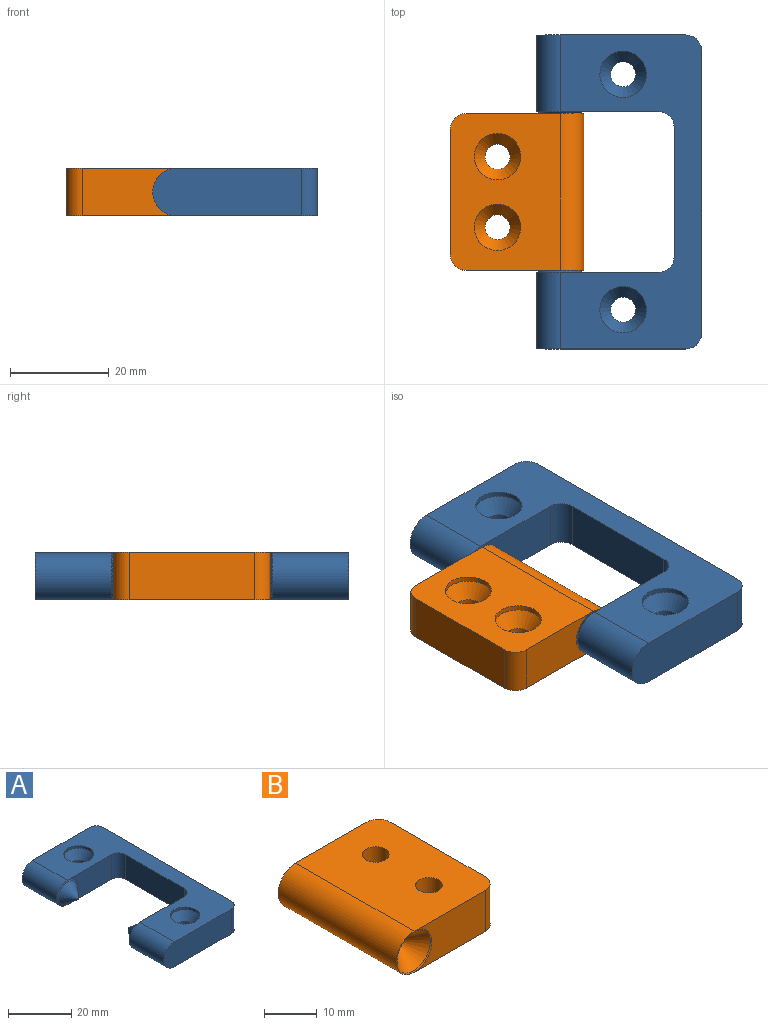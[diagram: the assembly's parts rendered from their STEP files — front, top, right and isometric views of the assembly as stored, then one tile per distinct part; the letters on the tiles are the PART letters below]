
ASSEMBLY  parts=2 mates=1
PART A: 26 faces, bbox 34.3x63.5x11.5 mm
  f0: plane 19.84x9.53mm, normal (0,-1,0), area 153.4mm2, adj f4,f6,f19,f23
  f1: plane 19.84x9.53mm, normal (0,1,0), area 153.4mm2, adj f4,f6,f18,f22
  f2: cylinder r=4.76mm len=15.48mm, axis (0,1,0), area 231.6mm2, adj f4,f6,f8,f19
  f3: cylinder r=4.76mm len=15.48mm, axis (0,1,0), area 231.6mm2, adj f4,f6,f7,f18
  f4: plane 63.5x28.58mm, normal (0,0,-1), area 1024.9mm2, adj f0,f1,f2,f3,f5,f7,f8,f9
  f5: plane 57.15x9.53mm, normal (1,0,0), area 544.4mm2, adj f4,f6,f24,f25
  f6: plane 63.5x28.58mm, normal (0,0,1), area 926.7mm2, adj f0,f1,f2,f3,f5,f7,f8,f9
  f7: plane 30.16x9.53mm, normal (0,-1,0), area 277.6mm2, adj f3,f4,f6,f25
  f8: plane 30.16x9.53mm, normal (0,1,0), area 277.6mm2, adj f2,f4,f6,f24
  f9: plane 26.19x9.53mm, normal (-1,0,0), area 249.5mm2, adj f4,f6,f22,f23
  f10: cylinder r=2.54mm len=5.43mm, axis (0,0,1), area 86.6mm2, adj f4,f11
  f11: cone r=4.7mm half-angle=35deg, axis (0,0,1), area 85.6mm2, adj f10,f12
  f12: cylinder r=4.7mm len=9.4mm, axis (0,0,1), area 30mm2, adj f6,f11
  f13: cylinder r=2.54mm len=5.43mm, axis (0,0,1), area 86.6mm2, adj f4,f14
  f14: cone r=4.7mm half-angle=35deg, axis (0,0,1), area 85.6mm2, adj f13,f15
  f15: cylinder r=4.7mm len=9.4mm, axis (0,0,1), area 30mm2, adj f6,f14
  f16: sphere r=0.4mm, area 0.4mm2, adj f17
  f17: cone r=4.15mm half-angle=40deg, axis (0,-1,0), area 83.9mm2, adj f16,f18
  f18: torus R=4.76mm, axis (0,1,0), area 19.3mm2, adj f1,f3,f17
  f19: torus R=4.76mm, axis (0,1,0), area 19.3mm2, adj f0,f2,f20
  f20: cone r=4.15mm half-angle=40deg, axis (0,1,0), area 83.9mm2, adj f19,f21
  f21: sphere r=0.4mm, area 0.4mm2, adj f20
  f22: cylinder r=3.17mm len=9.53mm, axis (0,0,-1), area 47.5mm2, adj f1,f4,f6,f9
  f23: cylinder r=3.17mm len=9.53mm, axis (0,0,1), area 47.5mm2, adj f0,f4,f6,f9
  f24: cylinder r=3.17mm len=9.53mm, axis (0,0,1), area 47.5mm2, adj f4,f5,f6,f8
  f25: cylinder r=3.17mm len=9.53mm, axis (0,0,-1), area 47.5mm2, adj f4,f5,f6,f7
PART B: 20 faces, bbox 27.7x31.8x10.9 mm
  f0: plane 25.4x9.53mm, normal (1,0,0), area 241.9mm2, adj f1,f3,f18,f19
  f1: plane 31.75x22.23mm, normal (0,0,1), area 660.8mm2, adj f0,f2,f4,f5,f8,f11,f18,f19
  f2: cylinder r=4.76mm len=31.75mm, axis (0,1,0), area 475mm2, adj f1,f3,f12,f17
  f3: plane 31.75x22.23mm, normal (0,0,-1), area 562.6mm2, adj f0,f2,f4,f5,f6,f9,f18,f19
  f4: plane 19.05x9.53mm, normal (0,-1,0), area 145.8mm2, adj f1,f3,f17,f19
  f5: plane 19.05x9.53mm, normal (0,1,0), area 145.8mm2, adj f1,f3,f12,f18
  f6: cylinder r=4.7mm len=9.4mm, axis (0,0,-1), area 30mm2, adj f3,f7
  f7: cone r=2.54mm half-angle=35deg, axis (0,0,-1), area 85.6mm2, adj f6,f8
  f8: cylinder r=2.54mm len=5.43mm, axis (0,0,-1), area 86.6mm2, adj f1,f7
  f9: cylinder r=4.7mm len=9.4mm, axis (0,0,-1), area 30mm2, adj f3,f10
  f10: cone r=2.54mm half-angle=35deg, axis (0,0,-1), area 85.6mm2, adj f9,f11
  f11: cylinder r=2.54mm len=5.43mm, axis (0,0,-1), area 86.6mm2, adj f1,f10
  f12: torus R=4.76mm, axis (0,-1,0), area 10mm2, adj f2,f5,f13
  f13: cone r=4.46mm half-angle=40deg, axis (0,1,0), area 95.3mm2, adj f12,f14
  f14: sphere r=0.79mm, area 1.4mm2, adj f13
  f15: sphere r=0.79mm, area 1.4mm2, adj f16
  f16: cone r=4.46mm half-angle=40deg, axis (0,-1,0), area 95.3mm2, adj f15,f17
  f17: torus R=4.76mm, axis (0,-1,0), area 10mm2, adj f2,f4,f16
  f18: cylinder r=3.17mm len=9.53mm, axis (0,0,1), area 47.5mm2, adj f0,f1,f3,f5
  f19: cylinder r=3.17mm len=9.53mm, axis (0,0,-1), area 47.5mm2, adj f0,f1,f3,f4
PLACE A t=(-16.36,0,4.76)mm
PLACE B rot(axis=(0,1,0),180deg) t=(-16.36,0,4.76)mm
MATE revolute A.f2 <-> B.f2  axis (0,-1,0) through (-16.36,16.27,4.76)mm
